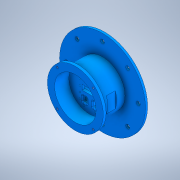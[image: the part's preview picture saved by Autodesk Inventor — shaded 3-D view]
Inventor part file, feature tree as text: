
AUTODESK INVENTOR PART (.ipt)
format: ipt  version: 2021 (Build 250183000, 183)  size: 380,928 bytes
history: native  units: mm
features: sketch x8, extrude x8, plane x4, fillet x2, other x1, hole x1
ambient origin geometry x8: Origin, YZ Plane, XZ Plane, XY Plane, X Axis, Y Axis, Z Axis, Center Point
bodies: Body1 (feature_tree)
feature tree (24):
  other  "Sólido1"
  sketch  "Boceto1"  dims[d0=32.0mm d1=50.0mm]
  extrude  "Extrusión1"  Depth=50.0mm
  plane  "Plano de trabajo1"
  extrude  "Extrusión2"  Depth=12.0mm
  sketch  "Boceto4"  dims[d14=2.2mm d16=2.2mm d18=2.2mm]
  extrude  "Extrusión4"  Depth=2.2mm
  fillet  "Empalme2"  Radius=2.2mm
  extrude  "Extrusión5"  Depth=2.2mm
  fillet  "Empalme3"  Radius=2.2mm
  sketch  "Boceto8"  dims[d21=2.2mm d22=2.2mm]
  plane  "Plano de trabajo3"
  sketch  "Boceto9"  dims[d23=2.2mm d24=27.0mm]
  extrude  "Extrusión12"  Depth=2.2mm
  plane  "Plano de trabajo5"
  hole  "Agujero1"  [1 undecoded]
  plane  "Plano de trabajo4"
  extrude  "Extrusión14"  Depth=16.0mm
  extrude  "Extrusión15"  Depth=6.5mm
  extrude  "Extrusión17"  Depth=8.0mm
  sketch  "Boceto2"  dims[d3=12.0mm d4=11.5mm]
  sketch  "Boceto3"  dims[d8=2.2mm d9=2.2mm d12=2.2mm]
  sketch  "Boceto11"  dims[d25=16.0mm d26=36.0mm]
  sketch  "Boceto12"  dims[d27=30.5mm d28=6.5mm d30=8.0mm d31=8.0mm d32=8.0mm d33=8.0mm d34=8.0mm d38=63.0mm d39=38.0mm d40=0.0mm d41=-24.0mm d42=58.0mm d43=4.0mm d44=0.0mm d47=63.0mm d55=4.0mm d56=4.0mm d57=0.0mm d58=2.0mm d60=2.0mm d61=11.65mm d62=10.5mm d63=7.0mm d64=21.0mm d68=2.2mm d72=5.6mm d75=4.0mm d77=4.4mm d79=5.6mm d80=0.8mm d81=0.8mm d82=26.0mm d83=0.0mm d84=2.0mm d103=4.0mm d104=4.0mm d105=4.0mm d106=4.0mm d107=4.0mm d108=4.0mm d109=4.0mm d110=4.0mm d112=8.0mm d113=50.0mm d114=50.0mm d115=50.0mm d116=50.0mm d117=50.0mm d118=50.0mm d119=50.0mm d124=9.734mm d125=2.5mm d126=120.0mm d127=5.5mm d128=5.5mm d129=5.5mm d130=5.5mm d131=5.5mm d132=5.5mm d133=5.5mm d134=5.5mm d135=50.0mm d136=7.25mm d137=50.0mm d138=50.0mm d139=50.0mm d140=50.0mm d141=50.0mm d142=50.0mm d143=50.0mm d145=25.0mm d146=8.0mm d149=15.0mm d150=0.0mm d154=1.5mm d155=40.0mm d157=360.0deg d159=2.85mm d160=7.0mm d161=4.0mm d162=2.0mm d163=90.0deg d164=10.4mm d165=0.0mm d166=35.0mm d167=12.5mm d168=2.0mm d169=0.0mm d170=3.0mm d171=0.0mm d174=58.0mm d175=5.0mm d176=0.0mm d147=0.5mm d148=0.872665mm d177=0.5mm d178=0.872665mm d179=0.5mm d180=0.872665mm]
note: 1 required parameter value undecoded (feature->parameter linkage not recoverable at this tier; creation-order binding heuristic only, values carry confidence <= 0.55)
